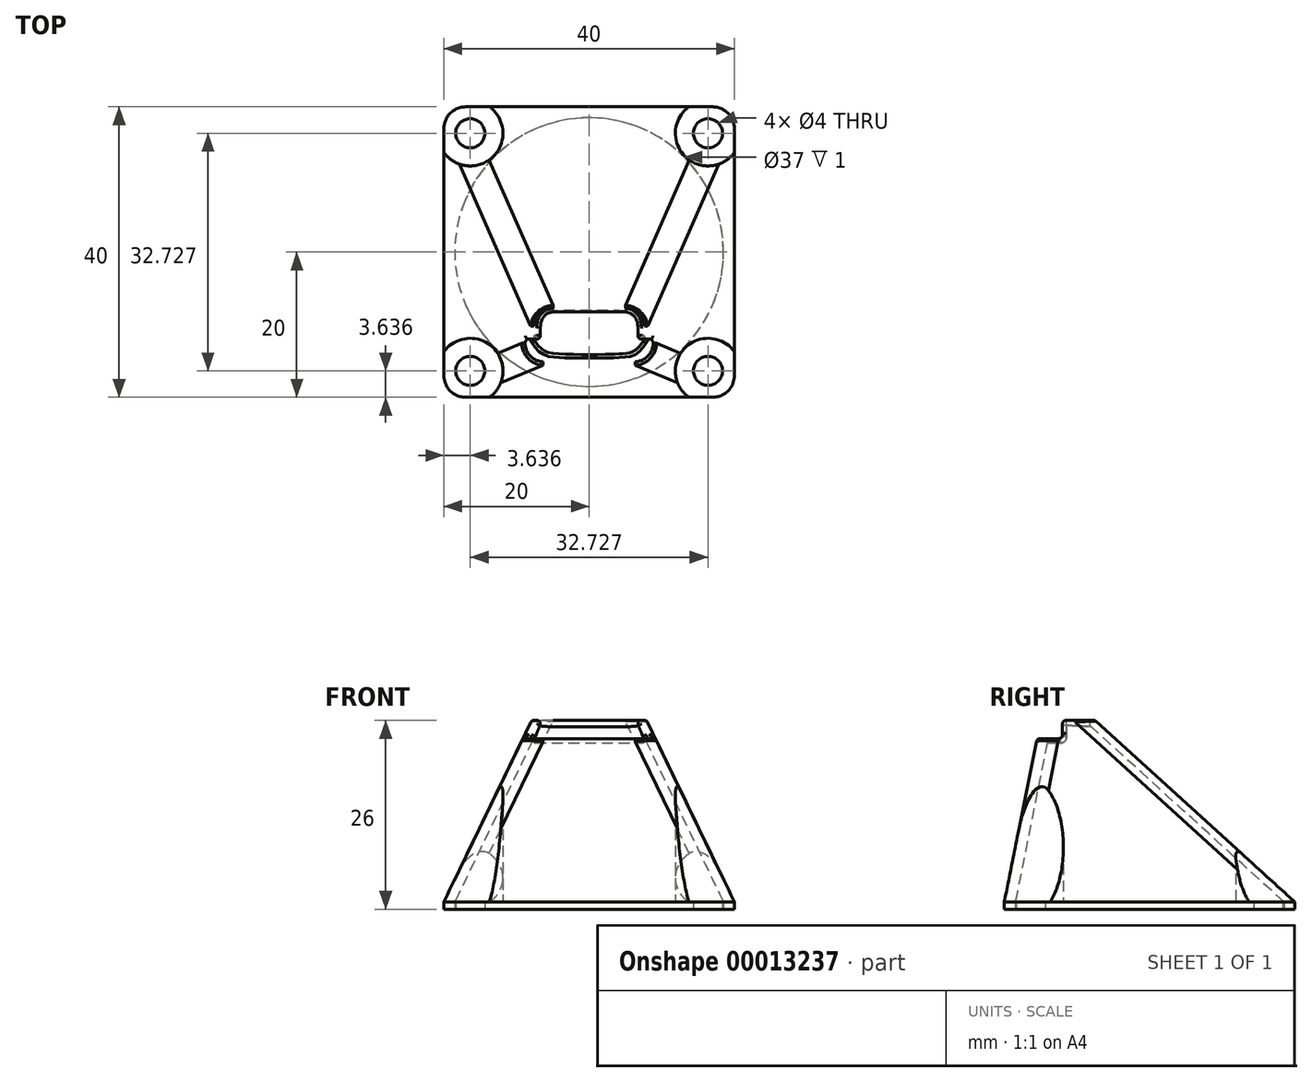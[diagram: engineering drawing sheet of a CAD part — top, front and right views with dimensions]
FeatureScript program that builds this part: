
annotation { "Feature Type Name" : "Feature", "Feature Type Description" : "" }
export const myFeature = defineFeature(function(context is Context, id is Id, definition is map)
    precondition{}
    {
        {
            var Q0;
            Q0=qCreatedBy(makeId("Top.planeOp"),FACE);
            var sketch = newSketch(context, id + "F0", { "sketchPlane" : qUnion([Q0])});
            skCircle(sketch, "E0", {"center": v(0, 0) * mm, "radius": 18.5 * mm});
            skLineSegment(sketch, "E1.bottom", {"start": v(-17, 20) * mm, "end": v(17, 20) * mm});
            skLineSegment(sketch, "E1.top", {"start": v(-17, -20) * mm, "end": v(17, -20) * mm});
            skLineSegment(sketch, "E1.left", {"start": v(-20, 17) * mm, "end": v(-20, -17) * mm});
            skLineSegment(sketch, "E1.right", {"start": v(20, 17) * mm, "end": v(20, -17) * mm});
            skLineSegment(sketch, "E2", {"start": v(-20, 20) * mm, "end": v(20, -20) * mm, "construction": true});
            skLineSegment(sketch, "E3", {"start": v(20, 20) * mm, "end": v(-20, -20) * mm, "construction": true});
            skCircle(sketch, "E4", {"center": v(-16.36, 16.36) * mm, "radius": 2 * mm});
            skCircle(sketch, "E5", {"center": v(-16.36, -16.36) * mm, "radius": 2 * mm});
            skCircle(sketch, "E6", {"center": v(16.36, -16.36) * mm, "radius": 2 * mm});
            skCircle(sketch, "E7", {"center": v(16.36, 16.36) * mm, "radius": 2 * mm});
            skLineSegment(sketch, "E8.bottom", {"start": v(-16.36, 16.36) * mm, "end": v(16.36, 16.36) * mm, "construction": true});
            skLineSegment(sketch, "E8.top", {"start": v(-16.36, -16.36) * mm, "end": v(16.36, -16.36) * mm, "construction": true});
            skLineSegment(sketch, "E8.left", {"start": v(-16.36, 16.36) * mm, "end": v(-16.36, -16.36) * mm, "construction": true});
            skLineSegment(sketch, "E8.right", {"start": v(16.36, 16.36) * mm, "end": v(16.36, -16.36) * mm, "construction": true});
            skPoint(sketch, "E9.visualSharp", {"position": v(-20, -20) * mm});
            skArc(sketch, "E9.filletArc", {"start": v(-20, -17) * mm, "mid": v(-19.12, -19.12) * mm, "end": v(-17, -20) * mm});
            skPoint(sketch, "E10.visualSharp", {"position": v(20, -20) * mm});
            skArc(sketch, "E10.filletArc", {"start": v(17, -20) * mm, "mid": v(19.12, -19.12) * mm, "end": v(20, -17) * mm});
            skPoint(sketch, "E11.visualSharp", {"position": v(20, 20) * mm});
            skArc(sketch, "E11.filletArc", {"start": v(20, 17) * mm, "mid": v(19.12, 19.12) * mm, "end": v(17, 20) * mm});
            skPoint(sketch, "E12.visualSharp", {"position": v(-20, 20) * mm});
            skArc(sketch, "E12.filletArc", {"start": v(-17, 20) * mm, "mid": v(-19.12, 19.12) * mm, "end": v(-20, 17) * mm});
            skPoint(sketch, "E13", {"position": v(-17.78, 17.78) * mm});
            skPoint(sketch, "E14", {"position": v(-19.12, 19.12) * mm});
            skSolve(sketch);
        }
        {
            var Q0;
            Q0=makeQuery(id+"F0.imprint","IMPRINT",FACE,{"disambiguationData":[TD([[makeQuery(id+"F0.imprint","IMPRINT",EDGE,{"derivedFrom":sQuery(id+"F0.wireOp",EDGE,"E0")}),-1.0]])]});
            extrude(context, id + "F1", {"entities" : qUnion([Q0]), "depth" : 1 * mm});
        }
        {
            var Q0;
            Q0=makeQuery(id+"F1.opExtrude","CAP_FACE",FACE,{"disambiguationData":[OSD([sQuery(id+"F0.wireOp",EDGE,"E0"),sQuery(id+"F0.wireOp",EDGE,"E1.bottom"),sQuery(id+"F0.wireOp",EDGE,"E1.top"),sQuery(id+"F0.wireOp",EDGE,"E1.left"),sQuery(id+"F0.wireOp",EDGE,"E1.right"),sQuery(id+"F0.wireOp",EDGE,"E4"),sQuery(id+"F0.wireOp",EDGE,"E5"),sQuery(id+"F0.wireOp",EDGE,"E6"),sQuery(id+"F0.wireOp",EDGE,"E7"),sQuery(id+"F0.wireOp",EDGE,"E9.filletArc"),sQuery(id+"F0.wireOp",EDGE,"E10.filletArc"),sQuery(id+"F0.wireOp",EDGE,"E11.filletArc"),sQuery(id+"F0.wireOp",EDGE,"E12.filletArc")])],"isStart":false});
            cPlane(context, id + "F2", {"entities" : qUnion([Q0]), "cplaneType" : CPlaneType.OFFSET, "offset" : 25 * mm, "width" : 150 * mm, "height" : 150 * mm});
        }
        {
            var Q0;
            Q0=makeQuery(id+"F1.opExtrude","CAP_FACE",FACE,{"disambiguationData":[OSD([sQuery(id+"F0.wireOp",EDGE,"E0"),sQuery(id+"F0.wireOp",EDGE,"E1.bottom"),sQuery(id+"F0.wireOp",EDGE,"E1.top"),sQuery(id+"F0.wireOp",EDGE,"E1.left"),sQuery(id+"F0.wireOp",EDGE,"E1.right"),sQuery(id+"F0.wireOp",EDGE,"E4"),sQuery(id+"F0.wireOp",EDGE,"E5"),sQuery(id+"F0.wireOp",EDGE,"E6"),sQuery(id+"F0.wireOp",EDGE,"E7"),sQuery(id+"F0.wireOp",EDGE,"E9.filletArc"),sQuery(id+"F0.wireOp",EDGE,"E10.filletArc"),sQuery(id+"F0.wireOp",EDGE,"E11.filletArc"),sQuery(id+"F0.wireOp",EDGE,"E12.filletArc")])],"isStart":false});
            var sketch = newSketch(context, id + "F3", { "sketchPlane" : qUnion([Q0])});
            skLineSegment(sketch, "E15.0.0", {"start": v(17, 20) * mm, "end": v(-17, 20) * mm});
            skArc(sketch, "E15.0.1", {"start": v(-17, 20) * mm, "mid": v(-19.12, 19.12) * mm, "end": v(-20, 17) * mm});
            skLineSegment(sketch, "E15.0.2", {"start": v(-20, 17) * mm, "end": v(-20, -17) * mm});
            skArc(sketch, "E15.0.3", {"start": v(-20, -17) * mm, "mid": v(-19.12, -19.12) * mm, "end": v(-17, -20) * mm});
            skLineSegment(sketch, "E15.0.4", {"start": v(-17, -20) * mm, "end": v(17, -20) * mm});
            skArc(sketch, "E15.0.5", {"start": v(17, -20) * mm, "mid": v(19.12, -19.12) * mm, "end": v(20, -17) * mm});
            skLineSegment(sketch, "E15.0.6", {"start": v(20, -17) * mm, "end": v(20, 17) * mm});
            skArc(sketch, "E15.0.7", {"start": v(20, 17) * mm, "mid": v(19.12, 19.12) * mm, "end": v(17, 20) * mm});
            skSolve(sketch);
        }
        {
            var Q0;
            Q0=qCreatedBy(id+"F2.planeOp",FACE);
            var sketch = newSketch(context, id + "F4", { "sketchPlane" : qUnion([Q0])});
            skLineSegment(sketch, "E16.bottom", {"start": v(-4.92, -7.5) * mm, "end": v(4.92, -7.5) * mm});
            skLineSegment(sketch, "E16.top", {"start": v(-4.92, -15) * mm, "end": v(4.92, -15) * mm});
            skPoint(sketch, "E17.visualSharp", {"position": v(-7.5, -7.5) * mm});
            skArc(sketch, "E17.filletArc", {"start": v(-4.92, -7.5) * mm, "mid": v(-7.05, -8.38) * mm, "end": v(-7.92, -10.5) * mm});
            skPoint(sketch, "E18.visualSharp", {"position": v(-7.5, -15) * mm});
            skArc(sketch, "E18.filletArc", {"start": v(-7.92, -12) * mm, "mid": v(-7.05, -14.12) * mm, "end": v(-4.92, -15) * mm});
            skPoint(sketch, "E19.visualSharp", {"position": v(7.5, -15) * mm});
            skArc(sketch, "E19.filletArc", {"start": v(4.92, -15) * mm, "mid": v(7.05, -14.12) * mm, "end": v(7.92, -12) * mm});
            skPoint(sketch, "E20.visualSharp", {"position": v(7.5, -7.5) * mm});
            skArc(sketch, "E20.filletArc", {"start": v(7.92, -10.5) * mm, "mid": v(7.05, -8.38) * mm, "end": v(4.92, -7.5) * mm});
            skLineSegment(sketch, "E21", {"start": v(0, 20) * mm, "end": v(0, -20) * mm, "construction": true});
            skPoint(sketch, "E22", {"position": v(0, -7.5) * mm});
            skLineSegment(sketch, "E23", {"start": v(-7.92, -10.5) * mm, "end": v(-7.92, -12) * mm});
            skLineSegment(sketch, "E24", {"start": v(7.92, -12) * mm, "end": v(7.92, -10.5) * mm});
            skPoint(sketch, "E25", {"position": v(0, -15) * mm});
            skSolve(sketch);
        }
        {
            var Q1;
            Q1 = qSketchRegion(id + "F3", true);
            var Q2;
            Q2 = qSketchRegion(id + "F4", true);
            loft(context, id + "F5", {"operationType" : NewBodyOperationType.ADD, "sheetProfilesArray" : [{ "sheetProfileEntities" : qUnion([Q1]) }, { "sheetProfileEntities" : qUnion([Q2]) }]});
        }
        {
            var Q0;
            Q0=makeQuery(id+"F4.imprint","IMPRINT",FACE,{"disambiguationData":[TD([[makeQuery(id+"F4.imprint","IMPRINT",EDGE,{"derivedFrom":sQuery(id+"F4.wireOp",EDGE,"E16.bottom")}),-1.0]])]});
            var sketch = newSketch(context, id + "F6", { "sketchPlane" : qUnion([Q0])});
            skFitSpline(sketch, "E26.0", {"points": [v(6.42, -10.5) * mm, v(6.42, -10.4) * mm, v(6.4, -10.2) * mm, v(6.3, -9.83) * mm, v(6.07, -9.5) * mm, v(5.76, -9.24) * mm, v(5.5, -9.1) * mm, v(5.22, -9.02) * mm, v(5.02, -9) * mm, v(4.92, -9) * mm]});
            skLineSegment(sketch, "E26.1", {"start": v(6.42, -12) * mm, "end": v(6.42, -10.5) * mm});
            skLineSegment(sketch, "E26.2", {"start": v(4.92, -9) * mm, "end": v(-4.92, -9) * mm});
            skFitSpline(sketch, "E26.3", {"points": [v(4.92, -13.5) * mm, v(5.02, -13.5) * mm, v(5.22, -13.48) * mm, v(5.6, -13.37) * mm, v(5.93, -13.14) * mm, v(6.18, -12.84) * mm, v(6.32, -12.58) * mm, v(6.4, -12.3) * mm, v(6.42, -12.1) * mm, v(6.42, -12) * mm]});
            skFitSpline(sketch, "E26.4", {"points": [v(-4.92, -9) * mm, v(-5.02, -9) * mm, v(-5.22, -9.02) * mm, v(-5.6, -9.13) * mm, v(-5.93, -9.36) * mm, v(-6.18, -9.66) * mm, v(-6.32, -9.92) * mm, v(-6.4, -10.2) * mm, v(-6.42, -10.4) * mm, v(-6.42, -10.5) * mm]});
            skLineSegment(sketch, "E26.5", {"start": v(-6.42, -10.5) * mm, "end": v(-6.42, -12) * mm});
            skFitSpline(sketch, "E26.6", {"points": [v(-6.42, -12) * mm, v(-6.42, -12.1) * mm, v(-6.4, -12.3) * mm, v(-6.3, -12.67) * mm, v(-6.07, -13) * mm, v(-5.76, -13.26) * mm, v(-5.5, -13.4) * mm, v(-5.22, -13.48) * mm, v(-5.02, -13.5) * mm, v(-4.92, -13.5) * mm]});
            skLineSegment(sketch, "E26.7", {"start": v(-4.92, -13.5) * mm, "end": v(4.92, -13.5) * mm});
            skSolve(sketch);
        }
        {
            var Q0;
            Q0=makeQuery(id+"F3.imprint","IMPRINT",FACE,{"disambiguationData":[TD([[makeQuery(id+"F3.imprint","IMPRINT",EDGE,{"derivedFrom":makeQuery(id+"F1.opExtrude","CAP_EDGE",EDGE,{"disambiguationData":[OSD([sQuery(id+"F0.wireOp",EDGE,"E0")])],"isStart":false})}),1.0]])]});
            var sketch = newSketch(context, id + "F7", { "sketchPlane" : qUnion([Q0])});
            skLineSegment(sketch, "E27", {"start": v(7.08, -17.1) * mm, "end": v(-7.08, 17.1) * mm});
            skLineSegment(sketch, "E28", {"start": v(-17.1, 7.08) * mm, "end": v(17.1, -7.08) * mm});
            skLineSegment(sketch, "E29", {"start": v(-7.08, -17.1) * mm, "end": v(7.08, 17.1) * mm});
            skLineSegment(sketch, "E30", {"start": v(17.1, 7.08) * mm, "end": v(-17.1, -7.08) * mm});
            skArc(sketch, "E31", {"start": v(-17.1, -7.08) * mm, "mid": v(-13.08, -13.08) * mm, "end": v(-7.08, -17.1) * mm});
            skArc(sketch, "E32", {"start": v(-17.1, 7.08) * mm, "mid": v(-18.5, 0) * mm, "end": v(-17.1, -7.08) * mm});
            skArc(sketch, "E33", {"start": v(-7.08, 17.1) * mm, "mid": v(-13.08, 13.08) * mm, "end": v(-17.1, 7.08) * mm});
            skLineSegment(sketch, "E34", {"start": v(7.08, 17.1) * mm, "end": v(7.08, 17.1) * mm});
            skArc(sketch, "E35", {"start": v(17.1, 7.08) * mm, "mid": v(7.08, 17.1) * mm, "end": v(-7.08, 17.1) * mm});
            skArc(sketch, "E36", {"start": v(17.1, -7.08) * mm, "mid": v(18.5, 0) * mm, "end": v(17.1, 7.08) * mm});
            skArc(sketch, "E37", {"start": v(7.08, -17.1) * mm, "mid": v(13.08, -13.08) * mm, "end": v(17.1, -7.08) * mm});
            skArc(sketch, "E38", {"start": v(-7.08, -17.1) * mm, "mid": v(0, -18.5) * mm, "end": v(7.08, -17.1) * mm});
            skLineSegment(sketch, "E39", {"start": v(11.85, 0) * mm, "end": v(-11.85, 0) * mm});
            skSolve(sketch);
        }
        {
            var Q0;
            Q0=makeQuery(id+"F3.imprint","IMPRINT",FACE,{"disambiguationData":[TD([[makeQuery(id+"F3.imprint","IMPRINT",EDGE,{"derivedFrom":makeQuery(id+"F1.opExtrude","CAP_EDGE",EDGE,{"disambiguationData":[OSD([sQuery(id+"F0.wireOp",EDGE,"E0")])],"isStart":false})}),1.0]])]});
            var sketch = newSketch(context, id + "F8", { "sketchPlane" : qUnion([Q0])});
            skCircle(sketch, "E40", {"center": v(-16.36, 16.36) * mm, "radius": 4.5 * mm});
            skCircle(sketch, "E41", {"center": v(16.36, 16.36) * mm, "radius": 4.5 * mm});
            skCircle(sketch, "E42", {"center": v(16.36, -16.36) * mm, "radius": 4.5 * mm});
            skCircle(sketch, "E43", {"center": v(-16.36, -16.36) * mm, "radius": 4.5 * mm});
            skSolve(sketch);
        }
        {
            var Q0;
            Q0 = qSketchRegion(id + "F8", true);
            extrude(context, id + "F9", {"entities" : qUnion([Q0]), "operationType" : NewBodyOperationType.REMOVE, "endBound" : BoundingType.THROUGH_ALL, "depth" : 30.1 * mm});
        }
        {
            var Q1;
            Q1=makeQuery(id+"F6.imprint","IMPRINT",FACE,{"disambiguationData":[TD([[makeQuery(id+"F6.imprint","IMPRINT",EDGE,{"derivedFrom":sQuery(id+"F6.wireOp",EDGE,"E26.0")}),1.0]])]});
            var Q2;
            Q2 = qSketchRegion(id + "F7", true);
            var Q3;
            Q3=sQuery(id+"F6.wireOp",VERTEX,"E26.7.start");
            var Q4;
            Q4=sQuery(id+"F7.wireOp",VERTEX,"E38.start");
            loft(context, id + "F10", {"operationType" : NewBodyOperationType.REMOVE, "sheetProfilesArray" : [{ "sheetProfileEntities" : qUnion([Q1]) }, { "sheetProfileEntities" : qUnion([Q2]) }], "matchConnections" : true, "connections" : [{ "connectionEntities" : qUnion([Q3, Q4]), "connectionEdgeQueries" : qUnion([]), "connectionEdgeParameters" : [] }]});
        }
        {
            var Q0;
            Q0=makeQuery(id+"F5.opLoft","CAP_FACE",FACE,{"disambiguationData":[OSD([makeQuery(id+"F4.imprint","IMPRINT",FACE,{"disambiguationData":[TD([[makeQuery(id+"F4.imprint","IMPRINT",EDGE,{"derivedFrom":sQuery(id+"F4.wireOp",EDGE,"E16.bottom")}),-1.0]])]})])],"isStart":true});
            var sketch = newSketch(context, id + "F11", { "sketchPlane" : qUnion([Q0])});
            skLineSegment(sketch, "E44.bottom", {"start": v(11.86, -20) * mm, "end": v(-11.86, -20) * mm});
            skLineSegment(sketch, "E44.top", {"start": v(11.86, -12) * mm, "end": v(-11.86, -12) * mm});
            skLineSegment(sketch, "E44.left", {"start": v(11.86, -20) * mm, "end": v(11.86, -12) * mm});
            skLineSegment(sketch, "E44.right", {"start": v(-11.86, -20) * mm, "end": v(-11.86, -12) * mm});
            skSolve(sketch);
        }
        {
            var Q0;
            Q0 = qSketchRegion(id + "F11", true);
            extrude(context, id + "F12", {"entities" : qUnion([Q0]), "operationType" : NewBodyOperationType.REMOVE, "oppositeDirection" : true, "depth" : 2.5 * mm});
        }
        {
            var Q0;
            Q0=makeQuery(id+"F12.boolean.opBoolean","COPY",FACE,{"derivedFrom":makeQuery(id+"F12.opExtrude","CAP_FACE",FACE,{"disambiguationData":[OSD([sQuery(id+"F11.wireOp",EDGE,"E44.bottom"),sQuery(id+"F11.wireOp",EDGE,"E44.top"),sQuery(id+"F11.wireOp",EDGE,"E44.left"),sQuery(id+"F11.wireOp",EDGE,"E44.right")])],"isStart":false})});
            var Q1;
            Q1=makeQuery(id+"F12.boolean.opBoolean","COPY",FACE,{"disambiguationData":[OD(0.0)],"derivedFrom":makeQuery(id+"F12.opExtrude","SWEPT_FACE",FACE,{"disambiguationData":[OSD([sQuery(id+"F11.wireOp",EDGE,"E44.top")])]})});
            var Q2;
            Q2=makeQuery(id+"F5.opLoft","CAP_FACE",FACE,{"disambiguationData":[OSD([makeQuery(id+"F4.imprint","IMPRINT",FACE,{"disambiguationData":[TD([[makeQuery(id+"F4.imprint","IMPRINT",EDGE,{"derivedFrom":sQuery(id+"F4.wireOp",EDGE,"E16.bottom")}),-1.0]])]})])],"isStart":true});
            var Q3;
            Q3=makeQuery(id+"F12.boolean.opBoolean","COPY",FACE,{"disambiguationData":[OD(1.0)],"derivedFrom":makeQuery(id+"F12.opExtrude","SWEPT_FACE",FACE,{"disambiguationData":[OSD([sQuery(id+"F11.wireOp",EDGE,"E44.top")])]})});
            fillet(context, id + "F13", {"entities" : qUnion([Q0, Q1, Q2, Q3]), "radius" : .5 * mm, "tangentPropagation" : true, "allowEdgeOverflow" : false});
        }
    });
